# Revit family: NBS_DudleyIndustriesLimited_SoapDpnsrs_AntiLigature_1LitreSoapDispenser
name_source: partatom
category: Specialty Equipment
revit_build: Autodesk Revit 2017 (Build: 20171027_0315(x64)
units: mm (PartAtom-declared; Revit-internal decimal feet)

## family parameters
Cut with Voids When Loaded = No
Host = Face
Part Type = Normal
Room Calculation Point = No
Round Connector Dimension = Use Diameter
Shared = No

## types (1)
- AntiLigature_1 LitreSoapDispenser
    AssetType = Fixed
    BIMObjectName = NBS_DudleyIndustriesLimited_SoapDispensers_AntiLigature_1LitreSoapDispenser
    Category = Pr_40_70_22_81:Soap dispensers
    Color = Chrome
    Default Elevation = 1200 mm
    Description = 1 litre soap dispenser
    DispenserCasingMaterial = NBS_Concept
    DurationUnit = year
    Features = No sharp edges or corners, robust and durable, works in conjunction with the Wall Plates 50062SS(brished stainless steel) 50062BL (blue) and 50062WH (white) to provide an anti-ligature solution for high risk areas
    Finish = Brushed
    Form = Wall mounted
    HandPushMaterial = NBS_Concept
    IfcExportAs = IfcSanitaryTerminalType
    IfcExportType = UNDEFINED
    ManufacturerName = Dudley Industries Limited
    ManufacturerURL = https://www.dudleyindustries.com
    Material = Stainless steel
    MaterialsBody = Stainless steel
    ModelNumber = 50060SS
    ModelReference = Anti-Ligature: 1 Litre Soap Dispenser
    NBSCertification = www.nationalbimlibrary.com/cert/w14r0ozi
    NBSDescription = Soap dispensers
    NBSReference = 45-35-72/358
    Name = SoapDispensers_Anti-Ligature:1LitreSoapDispenser_DudleyIndustriesLimited
    NominalDepth = 99 mm
    NominalHeight = 281 mm
    NominalLength = 0 mm  [stored 0 ft]
    NominalWidth = 191 mm
    NozzleMaterial = NBS_Concept
    Operation = Manual push operation
    PackingCarton = 1 piece
    PackingPallet = 150 pieces
    ProductInformation = http://dudleyindustries.com
    Shape = Rectangle
    Size = 115 x 281 x 99 mm
    Status = UNSET
    Uniclass2015Code = Pr_40_70_22_81
    Uniclass2015Title = Soap dispensers
    Uniclass2015Version = Products v1.11
    Version = 1
    WarrantyDurationUnit = year
    Weight = 1.8 kg

note: [stored X ft] marks values corroborated as IEEE doubles in the binary element streams (Revit-internal decimal feet)

## geometry (parser evidence)
native form markers: Sweep x2
no freeform markers — native parametric forms only
